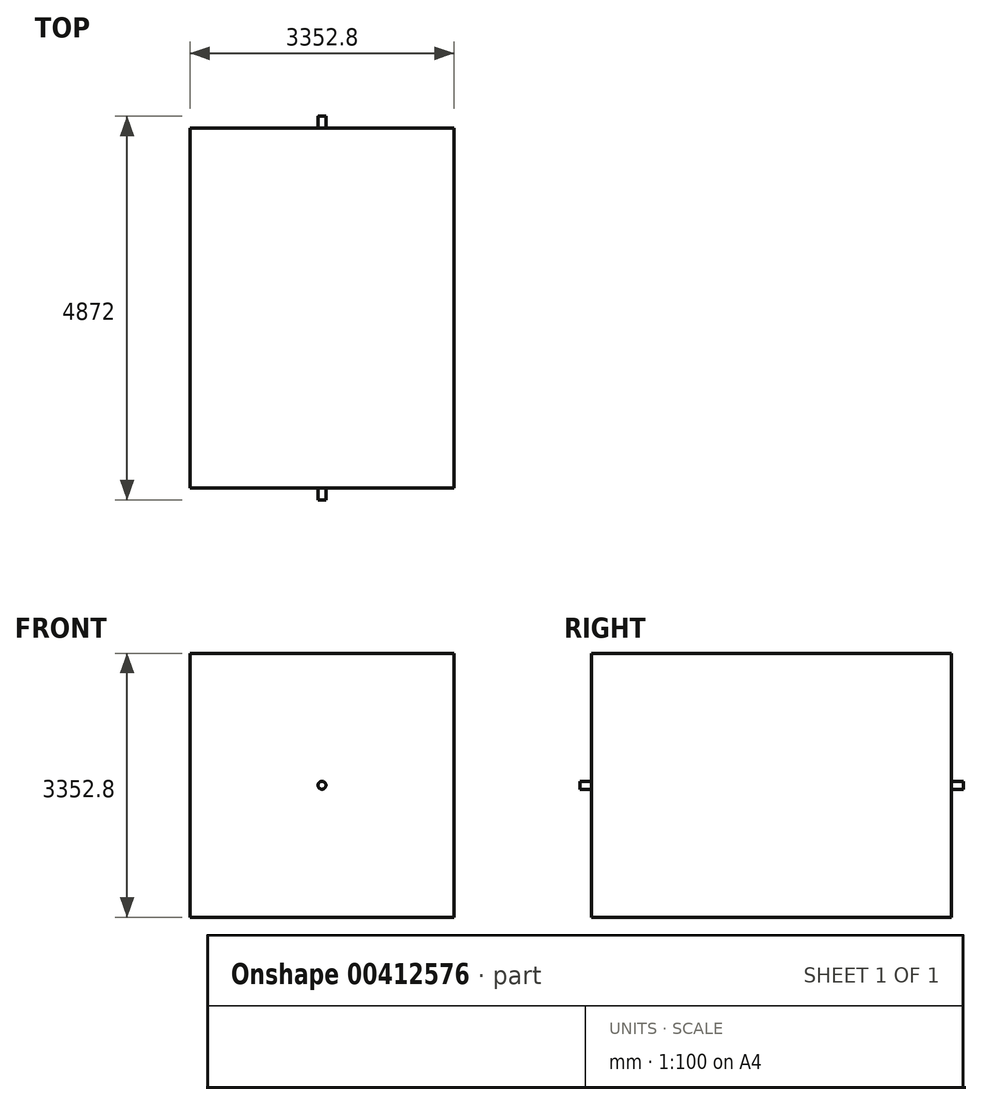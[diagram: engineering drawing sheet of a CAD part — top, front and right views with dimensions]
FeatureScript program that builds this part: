
annotation { "Feature Type Name" : "Feature", "Feature Type Description" : "" }
export const myFeature = defineFeature(function(context is Context, id is Id, definition is map)
    precondition{}
    {
        {
            var Q0;
            Q0=qCreatedBy(makeId("Front.planeOp"),FACE);
            var sketch = newSketch(context, id + "F0", { "sketchPlane" : qUnion([Q0])});
            skLineSegment(sketch, "E0.bottom", {"start": v(1676.4, 1676.4) * mm, "end": v(-1676.4, 1676.4) * mm});
            skLineSegment(sketch, "E0.top", {"start": v(1676.4, -1676.4) * mm, "end": v(-1676.4, -1676.4) * mm});
            skLineSegment(sketch, "E0.left", {"start": v(1676.4, 1676.4) * mm, "end": v(1676.4, -1676.4) * mm});
            skLineSegment(sketch, "E0.right", {"start": v(-1676.4, 1676.4) * mm, "end": v(-1676.4, -1676.4) * mm});
            skPoint(sketch, "E0.middle", {"position": v(0, 0) * mm});
            skSolve(sketch);
        }
        {
            var Q0;
            Q0 = qSketchRegion(id + "F0", true);
            extrude(context, id + "F1", {"entities" : qUnion([Q0]), "depth" : 4572 * mm});
        }
        {
            var Q0;
            Q0=makeQuery(id+"F1.opExtrude","CAP_FACE",FACE,{"disambiguationData":[OSD([sQuery(id+"F0.wireOp",EDGE,"E0.bottom"),sQuery(id+"F0.wireOp",EDGE,"E0.top"),sQuery(id+"F0.wireOp",EDGE,"E0.left"),sQuery(id+"F0.wireOp",EDGE,"E0.right")])],"isStart":true});
            var sketch = newSketch(context, id + "F2", { "sketchPlane" : qUnion([Q0])});
            skCircle(sketch, "E1", {"center": v(0, 0) * mm, "radius": 50 * mm});
            skSolve(sketch);
        }
        {
            var Q0;
            Q0 = qSketchRegion(id + "F2", true);
            extrude(context, id + "F3", {"entities" : qUnion([Q0]), "operationType" : NewBodyOperationType.ADD, "depth" : 150 * mm});
        }
        {
            var Q0;
            Q0=makeQuery(id+"F1.opExtrude","CAP_FACE",FACE,{"disambiguationData":[OSD([sQuery(id+"F0.wireOp",EDGE,"E0.bottom"),sQuery(id+"F0.wireOp",EDGE,"E0.top"),sQuery(id+"F0.wireOp",EDGE,"E0.left"),sQuery(id+"F0.wireOp",EDGE,"E0.right")])],"isStart":false});
            var sketch = newSketch(context, id + "F4", { "sketchPlane" : qUnion([Q0])});
            skCircle(sketch, "E2", {"center": v(0, 0) * mm, "radius": 50 * mm});
            skSolve(sketch);
        }
        {
            var Q0;
            Q0 = qSketchRegion(id + "F4", true);
            extrude(context, id + "F5", {"entities" : qUnion([Q0]), "operationType" : NewBodyOperationType.ADD, "depth" : 150 * mm});
        }
    });
